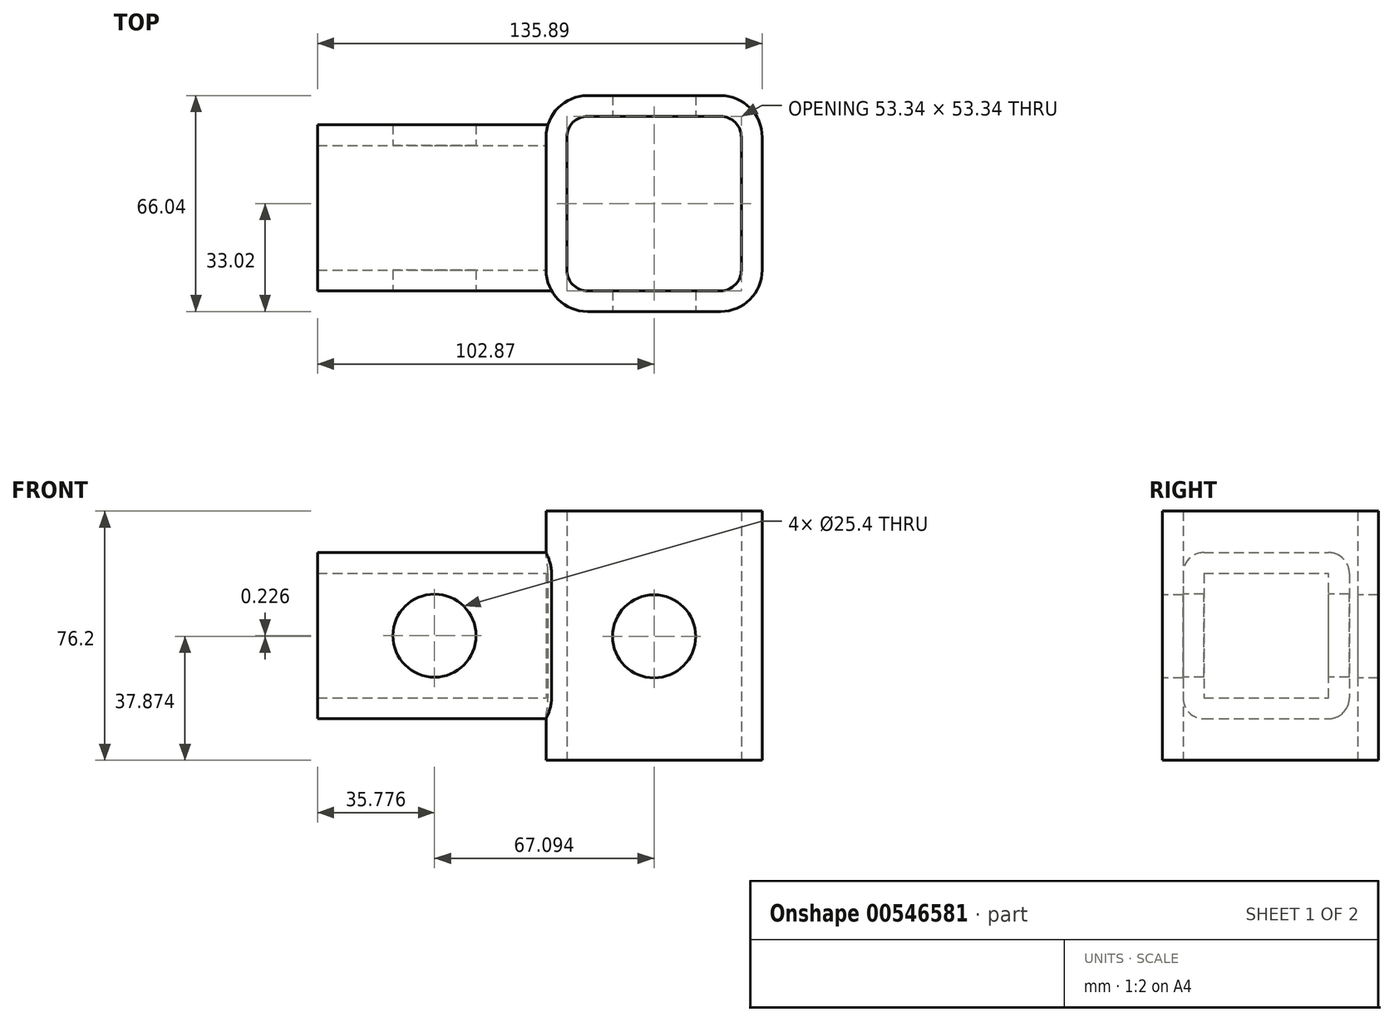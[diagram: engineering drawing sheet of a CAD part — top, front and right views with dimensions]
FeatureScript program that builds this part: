
annotation { "Feature Type Name" : "Feature", "Feature Type Description" : "" }
export const myFeature = defineFeature(function(context is Context, id is Id, definition is map)
    precondition{}
    {
        {
            var Q0;
            Q0=qCreatedBy(makeId("Top.planeOp"),FACE);
            var sketch = newSketch(context, id + "F0", { "sketchPlane" : qUnion([Q0])});
            skLineSegment(sketch, "E0.bottom", {"start": v(6.35, 0) * mm, "end": v(47, 0) * mm});
            skLineSegment(sketch, "E0.top", {"start": v(6.35, 53.34) * mm, "end": v(47, 53.34) * mm});
            skLineSegment(sketch, "E0.left", {"start": v(0, 6.35) * mm, "end": v(0, 47) * mm});
            skLineSegment(sketch, "E0.right", {"start": v(53.34, 6.35) * mm, "end": v(53.34, 47) * mm});
            skPoint(sketch, "E1.visualSharp", {"position": v(0, 53.34) * mm});
            skArc(sketch, "E1.filletArc", {"start": v(6.35, 53.34) * mm, "mid": v(1.86, 51.48) * mm, "end": v(0, 47) * mm});
            skPoint(sketch, "E2.visualSharp", {"position": v(53.34, 53.34) * mm});
            skArc(sketch, "E2.filletArc", {"start": v(53.34, 47) * mm, "mid": v(51.48, 51.48) * mm, "end": v(47, 53.34) * mm});
            skPoint(sketch, "E3.visualSharp", {"position": v(53.34, 0) * mm});
            skArc(sketch, "E3.filletArc", {"start": v(47, 0) * mm, "mid": v(51.48, 1.86) * mm, "end": v(53.34, 6.35) * mm});
            skPoint(sketch, "E4.visualSharp", {"position": v(0, 0) * mm});
            skArc(sketch, "E4.filletArc", {"start": v(0, 6.35) * mm, "mid": v(1.86, 1.86) * mm, "end": v(6.35, 0) * mm});
            skArc(sketch, "E5.0", {"start": v(6.35, 59.69) * mm, "mid": v(-2.63, 55.97) * mm, "end": v(-6.35, 47) * mm});
            skLineSegment(sketch, "E5.1", {"start": v(-6.35, 6.35) * mm, "end": v(-6.35, 47) * mm});
            skLineSegment(sketch, "E5.2", {"start": v(6.35, 59.69) * mm, "end": v(47, 59.69) * mm});
            skArc(sketch, "E5.3", {"start": v(-6.35, 6.35) * mm, "mid": v(-2.63, -2.63) * mm, "end": v(6.35, -6.35) * mm});
            skArc(sketch, "E5.4", {"start": v(59.69, 47) * mm, "mid": v(55.97, 55.97) * mm, "end": v(47, 59.69) * mm});
            skLineSegment(sketch, "E5.5", {"start": v(59.69, 6.35) * mm, "end": v(59.69, 47) * mm});
            skArc(sketch, "E5.6", {"start": v(47, -6.35) * mm, "mid": v(55.97, -2.63) * mm, "end": v(59.69, 6.35) * mm});
            skLineSegment(sketch, "E5.7", {"start": v(6.35, -6.35) * mm, "end": v(47, -6.35) * mm});
            skSolve(sketch);
        }
        {
            var Q0;
            Q0 = qSketchRegion(id + "F0", true);
            extrude(context, id + "F1", {"entities" : qUnion([Q0]), "depth" : 76.2 * mm, "offsetDistance" : 25.4 * mm, "symmetric" : true});
        }
        {
            var Q0;
            Q0=qCreatedBy(makeId("Front.planeOp"),FACE);
            var sketch = newSketch(context, id + "F2", { "sketchPlane" : qUnion([Q0])});
            skLineSegment(sketch, "E6.0", {"start": v(6.35, 38.1) * mm, "end": v(47, 38.1) * mm, "construction": true});
            skLineSegment(sketch, "E7", {"start": v(26.67, 38.1) * mm, "end": v(26.67, -38.55) * mm, "construction": true});
            skCircle(sketch, "E8", {"center": v(26.67, -0.23) * mm, "radius": 12.7 * mm});
            skSolve(sketch);
        }
        {
            var Q0;
            Q0 = qSketchRegion(id + "F2", true);
            extrude(context, id + "F3", {"entities" : qUnion([Q0]), "operationType" : NewBodyOperationType.REMOVE, "endBound" : BoundingType.THROUGH_ALL, "oppositeDirection" : true, "depth" : 25.4 * mm, "offsetDistance" : 25.4 * mm, "hasSecondDirection" : true, "secondDirectionOppositeDirection" : false, "secondDirectionDepth" : 25.4 * mm});
        }
        {
            var Q0;
            Q0=qCreatedBy(makeId("Right.planeOp"),FACE);
            var sketch = newSketch(context, id + "F4", { "sketchPlane" : qUnion([Q0])});
            skLineSegment(sketch, "E9.0", {"start": v(59.69, 38.1) * mm, "end": v(59.69, -38.1) * mm});
            skLineSegment(sketch, "E10.0", {"start": v(-6.35, 38.1) * mm, "end": v(-6.35, -38.1) * mm});
            skLineSegment(sketch, "E11.bottom", {"start": v(44.45, 25.4) * mm, "end": v(6.35, 25.4) * mm});
            skLineSegment(sketch, "E11.top", {"start": v(44.45, -25.4) * mm, "end": v(6.35, -25.4) * mm});
            skLineSegment(sketch, "E11.left", {"start": v(50.8, 19.05) * mm, "end": v(50.8, -19.05) * mm});
            skLineSegment(sketch, "E11.right", {"start": v(0, 19.05) * mm, "end": v(0, -19.05) * mm});
            skPoint(sketch, "E12.visualSharp", {"position": v(50.8, 25.4) * mm});
            skArc(sketch, "E12.filletArc", {"start": v(50.8, 19.05) * mm, "mid": v(48.94, 23.54) * mm, "end": v(44.45, 25.4) * mm});
            skPoint(sketch, "E13.visualSharp", {"position": v(0, 25.4) * mm});
            skArc(sketch, "E13.filletArc", {"start": v(6.35, 25.4) * mm, "mid": v(1.86, 23.54) * mm, "end": v(0, 19.05) * mm});
            skPoint(sketch, "E14.visualSharp", {"position": v(0, -25.4) * mm});
            skArc(sketch, "E14.filletArc", {"start": v(0, -19.05) * mm, "mid": v(1.86, -23.54) * mm, "end": v(6.35, -25.4) * mm});
            skPoint(sketch, "E15.visualSharp", {"position": v(50.8, -25.4) * mm});
            skArc(sketch, "E15.filletArc", {"start": v(44.45, -25.4) * mm, "mid": v(48.94, -23.54) * mm, "end": v(50.8, -19.05) * mm});
            skLineSegment(sketch, "E16.0", {"start": v(44.45, 19.05) * mm, "end": v(6.35, 19.05) * mm});
            skLineSegment(sketch, "E16.1", {"start": v(44.45, 19.05) * mm, "end": v(44.45, -19.05) * mm});
            skLineSegment(sketch, "E16.2", {"start": v(44.45, -19.05) * mm, "end": v(6.35, -19.05) * mm});
            skLineSegment(sketch, "E16.3", {"start": v(6.35, 19.05) * mm, "end": v(6.35, -19.05) * mm});
            skLineSegment(sketch, "E17.0", {"start": v(6.35, 38.1) * mm, "end": v(47, 38.1) * mm, "construction": true});
            skLineSegment(sketch, "E18", {"start": v(26.67, 38.1) * mm, "end": v(26.67, -6.3) * mm, "construction": true});
            skSolve(sketch);
        }
        {
            var Q0;
            Q0 = qSketchRegion(id + "F4", true);
            extrude(context, id + "F5", {"entities" : qUnion([Q0]), "operationType" : NewBodyOperationType.ADD, "oppositeDirection" : true, "depth" : 76.2 * mm, "offsetDistance" : 25.4 * mm});
        }
        {
            var Q0;
            Q0=qCreatedBy(makeId("Front.planeOp"),FACE);
            var sketch = newSketch(context, id + "F6", { "sketchPlane" : qUnion([Q0])});
            skCircle(sketch, "E19", {"center": v(-40.42, 0) * mm, "radius": 12.7 * mm});
            skLineSegment(sketch, "E20.0", {"start": v(-76.2, 19.05) * mm, "end": v(-4.65, 19.05) * mm, "construction": true});
            skLineSegment(sketch, "E21", {"start": v(-40.42, 19.05) * mm, "end": v(-40.42, -19.34) * mm, "construction": true});
            skSolve(sketch);
        }
        {
            var Q0;
            Q0 = qSketchRegion(id + "F6", true);
            extrude(context, id + "F7", {"entities" : qUnion([Q0]), "operationType" : NewBodyOperationType.REMOVE, "endBound" : BoundingType.THROUGH_ALL, "oppositeDirection" : true, "depth" : 25.4 * mm, "offsetDistance" : 25.4 * mm});
        }
    });
